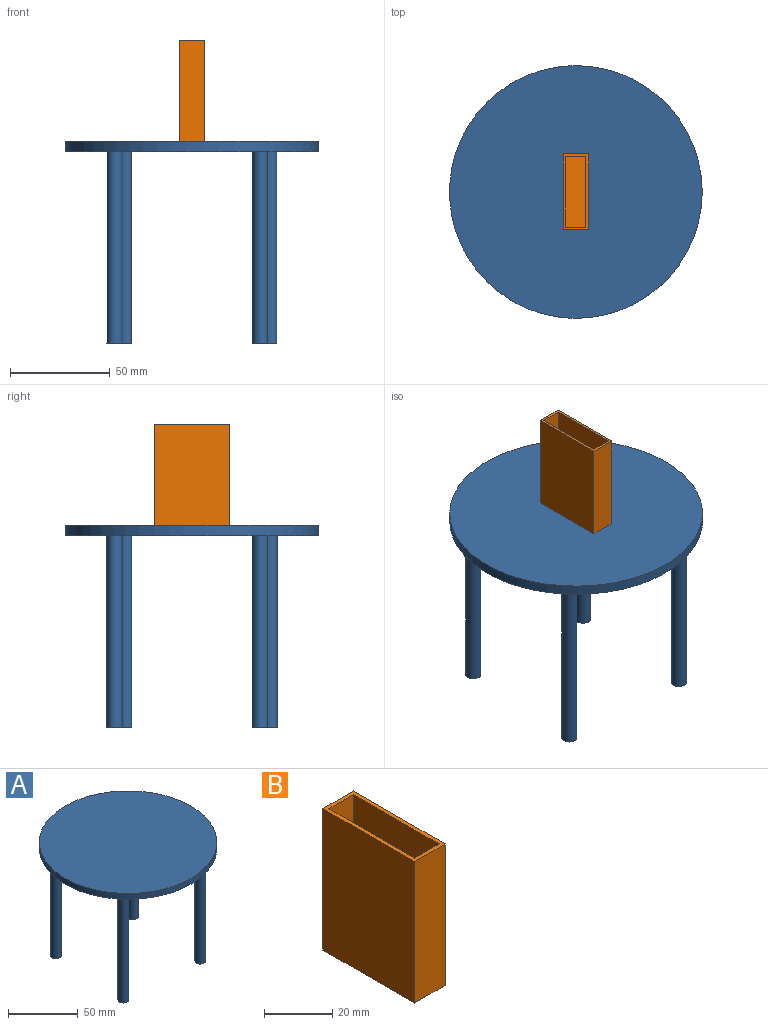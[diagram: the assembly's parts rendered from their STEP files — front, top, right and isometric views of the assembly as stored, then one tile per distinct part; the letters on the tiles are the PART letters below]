
ASSEMBLY  parts=2 mates=1
PART A: 11 faces, bbox 127x127x101.6 mm
  f0: cylinder r=63.5mm len=127mm, axis (0,0,-1), area 2026.8mm2, adj f1,f2
  f1: plane 127x127mm, normal (0,0,1), area 12667.7mm2, adj f0
  f2: plane 127x127mm, normal (0,0,-1), area 12485.3mm2, adj f0,f3,f5,f7,f9
  f3: cylinder r=3.81mm len=96.52mm, axis (0,0,1), area 2310.6mm2, adj f2,f4
  f4: plane 7.62x7.62mm, normal (0,0,-1), area 45.6mm2, adj f3
  f5: cylinder r=3.81mm len=96.52mm, axis (0,0,1), area 2310.6mm2, adj f2,f6
  f6: plane 7.62x7.62mm, normal (0,0,-1), area 45.6mm2, adj f5
  f7: cylinder r=3.81mm len=96.52mm, axis (0,0,1), area 2310.6mm2, adj f2,f8
  f8: plane 7.62x7.62mm, normal (0,0,-1), area 45.6mm2, adj f7
  f9: cylinder r=3.81mm len=96.52mm, axis (0,0,1), area 2310.6mm2, adj f2,f10
  f10: plane 7.62x7.62mm, normal (0,0,-1), area 45.6mm2, adj f9
PART B: 11 faces, bbox 12.7x38.1x50.8 mm
  f0: plane 50.8x12.7mm, normal (0,1,0), area 645.2mm2, adj f1,f3,f4,f5
  f1: plane 50.8x38.1mm, normal (-1,0,0), area 1935.5mm2, adj f0,f2,f4,f5
  f2: plane 50.8x12.7mm, normal (0,-1,0), area 645.2mm2, adj f1,f3,f4,f5
  f3: plane 50.8x38.1mm, normal (1,0,0), area 1935.5mm2, adj f0,f2,f4,f5
  f4: plane 38.1x12.7mm, normal (0,0,1), area 122.6mm2, adj f0,f1,f2,f3,f7,f8,f9,f10
  f5: plane 38.1x12.7mm, normal (0,0,-1), area 483.9mm2, adj f0,f1,f2,f3
  f6: plane 35.56x10.16mm, normal (0,0,1), area 361.3mm2, adj f7,f8,f9,f10
  f7: plane 49.53x35.56mm, normal (1,0,0), area 1761.3mm2, adj f4,f6,f8,f9
  f8: plane 49.53x10.16mm, normal (0,-1,0), area 503.2mm2, adj f4,f6,f7,f10
  f9: plane 49.53x10.16mm, normal (0,1,0), area 503.2mm2, adj f4,f6,f7,f10
  f10: plane 49.53x35.56mm, normal (-1,0,0), area 1761.3mm2, adj f4,f6,f8,f9
PLACE A t=(-36.68,-54,-3.51)mm
PLACE B t=(-11.96,-56.52,1.57)mm
MATE planar B.f5 <-> A.f0  axis (0,0,-1) through (-36.68,-54,1.57)mm
